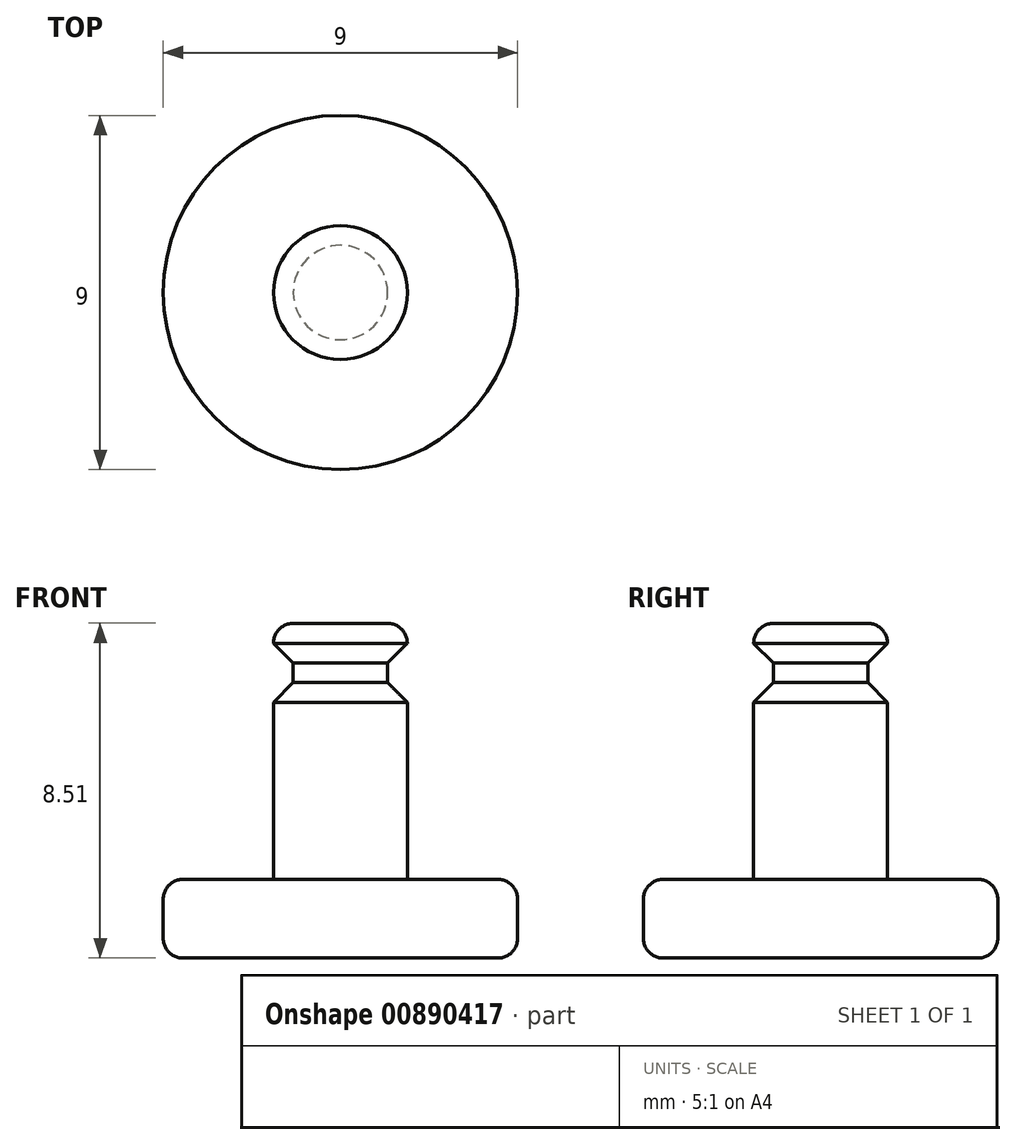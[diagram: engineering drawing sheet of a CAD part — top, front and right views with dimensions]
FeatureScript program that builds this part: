
annotation { "Feature Type Name" : "Feature", "Feature Type Description" : "" }
export const myFeature = defineFeature(function(context is Context, id is Id, definition is map)
    precondition{}
    {
        {
            var Q0;
            Q0=qCreatedBy(makeId("Front.planeOp"),FACE);
            var sketch = newSketch(context, id + "F0", { "sketchPlane" : qUnion([Q0])});
            skLineSegment(sketch, "E0", {"start": v(0, 0) * mm, "end": v(4.5, 0) * mm});
            skLineSegment(sketch, "E1", {"start": v(4.5, 0) * mm, "end": v(4.5, 2) * mm});
            skLineSegment(sketch, "E2", {"start": v(4.5, 2) * mm, "end": v(1.7, 2) * mm});
            skLineSegment(sketch, "E3", {"start": v(1.7, 2) * mm, "end": v(1.7, 6.5) * mm});
            skLineSegment(sketch, "E4", {"start": v(1.2, 7.5) * mm, "end": v(1.7, 8) * mm});
            skLineSegment(sketch, "E5", {"start": v(1, 8.5) * mm, "end": v(0, 8.5) * mm});
            skLineSegment(sketch, "E6", {"start": v(0, 8.5) * mm, "end": v(0, 0) * mm});
            skLineSegment(sketch, "E7", {"start": v(1.7, 8) * mm, "end": v(1.7, 8.5) * mm});
            skLineSegment(sketch, "E8", {"start": v(1.7, 8.5) * mm, "end": v(1, 8.5) * mm});
            skLineSegment(sketch, "E9", {"start": v(1.7, 6.5) * mm, "end": v(1.2, 7) * mm});
            skLineSegment(sketch, "E10", {"start": v(1.2, 7.5) * mm, "end": v(1.2, 7) * mm});
            skSolve(sketch);
        }
        {
            var Q0;
            Q0 = qSketchRegion(id + "F0", true);
            var Q1;
            Q1=sQuery(id+"F0.wireOp",EDGE,"E6");
            revolve(context, id + "F1", {"surfaceOperationType" : NewSurfaceOperationType.NEW, "entities" : qUnion([Q0]), "axis" : qUnion([Q1]), "revolveType" : RevolveType.FULL});
        }
        {
            var Q0;
            Q0=makeQuery(id+"F1.opRevolve","SWEPT_EDGE",EDGE,{"disambiguationData":[OSD([sQuery(id+"F0.wireOp",EDGE,"E7"),sQuery(id+"F0.wireOp",EDGE,"E8")])]});
            fillet(context, id + "F2", {"entities" : qUnion([Q0]), "radius" : 0.5 * mm, "tangentPropagation" : true, "allowEdgeOverflow" : false});
        }
        {
            var Q0;
            Q0=makeQuery(id+"F1.opRevolve","SWEPT_EDGE",EDGE,{"disambiguationData":[OSD([sQuery(id+"F0.wireOp",EDGE,"E0"),sQuery(id+"F0.wireOp",EDGE,"E1")])]});
            var Q1;
            Q1=makeQuery(id+"F1.opRevolve","SWEPT_EDGE",EDGE,{"disambiguationData":[OSD([sQuery(id+"F0.wireOp",EDGE,"E1"),sQuery(id+"F0.wireOp",EDGE,"E2")])]});
            fillet(context, id + "F3", {"entities" : qUnion([Q0, Q1]), "radius" : 0.5 * mm, "tangentPropagation" : true, "allowEdgeOverflow" : false});
        }
    });
